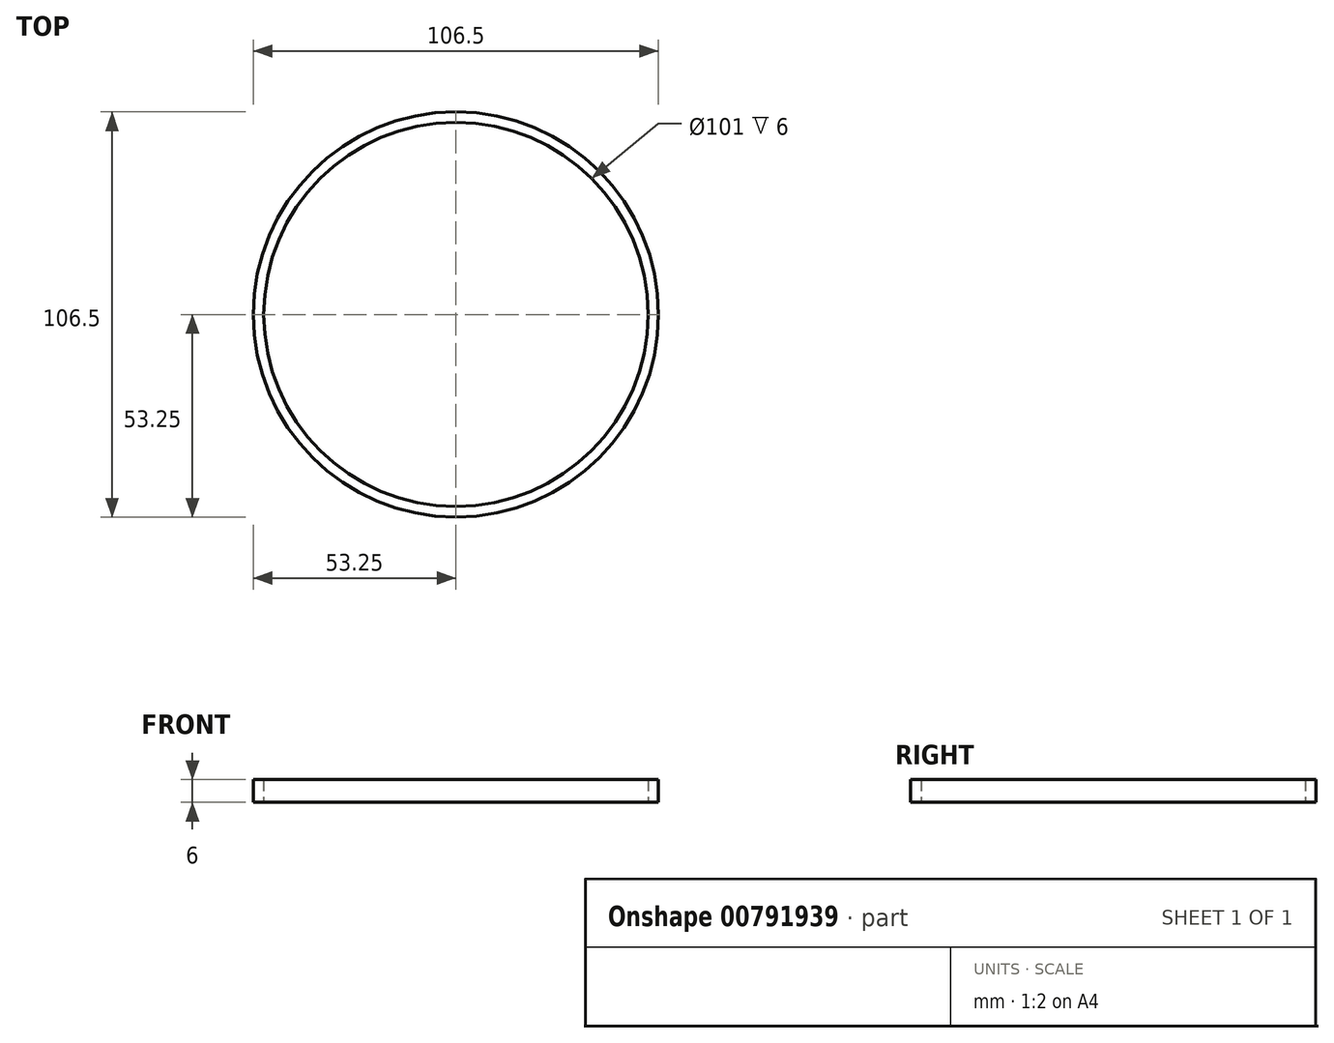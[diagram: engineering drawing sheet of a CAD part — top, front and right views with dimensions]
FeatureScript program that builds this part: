
annotation { "Feature Type Name" : "Feature", "Feature Type Description" : "" }
export const myFeature = defineFeature(function(context is Context, id is Id, definition is map)
    precondition{}
    {
        {
            var Q0;
            Q0=qCreatedBy(makeId("Top.planeOp"),FACE);
            var sketch = newSketch(context, id + "F0", { "sketchPlane" : qUnion([Q0])});
            skCircle(sketch, "E0", {"center": v(0, 0) * mm, "radius": 50.5 * mm});
            skCircle(sketch, "E1", {"center": v(0, 0) * mm, "radius": 53.25 * mm});
            skSolve(sketch);
        }
        {
            var Q0;
            Q0 = qSketchRegion(id + "F0", true);
            extrude(context, id + "F1", {"entities" : qUnion([Q0]), "depth" : 6 * mm, "offsetDistance" : 25.4 * mm});
        }
    });
